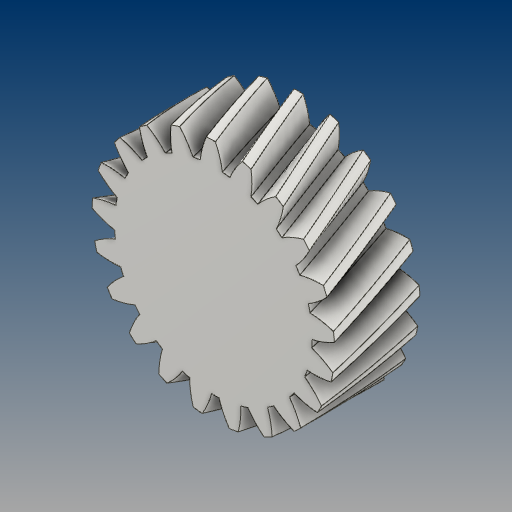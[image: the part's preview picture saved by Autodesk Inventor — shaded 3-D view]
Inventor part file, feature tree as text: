
AUTODESK INVENTOR PART (.ipt)
format: ipt  version: 2021 (Build 250183000, 183)  size: 506,880 bytes
history: native  units: mm (DEFAULTED — no unit token found)
features: plane x3, other x3, sketch x2, extrude x1
ambient origin geometry x8: Origin, YZ Plane, XZ Plane, XY Plane, X Axis, Y Axis, Z Axis, Center Point
bodies: Solid1 (feature_tree)
feature tree (9):
  extrude  "Extrusion1"  Depth=15.0mm TaperAngle=0.0deg
  plane  "Work Plane2"
  plane  "Work Plane8"
  plane  "Work Plane9"
  other  "Spur Gear"
  sketch  "Sketch1"  dims[d0=42.592282mm d1=15.0mm d2=0.0mm]
  sketch  "Sketch2"  dims[d3=39.108533mm d4=10.0mm d5=0.0mm d16=60.0mm d17=0.0mm d34=1.495997mm d39=0.0mm d41=0.0mm d43=60.0mm d46=60.0mm d47=0.0mm d48=0.0mm]
  other  "Srf1"
  other  "Pitch Diameter"
